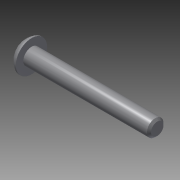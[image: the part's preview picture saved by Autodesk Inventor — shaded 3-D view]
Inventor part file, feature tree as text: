
AUTODESK INVENTOR PART (.ipt)
format: ipt  version: 2015 (Build 190159000, 159)  size: 118,784 bytes
history: native  units: in
note: dims shown in document units (in); Inventor stores cm internally (conversion verified against a paired STEP export)
features: other x3, extrude x1, chamfer x1, imported_body x1, sketch x1
ambient origin geometry x8: Origin, YZ Plane, XZ Plane, XY Plane, X Axis, Y Axis, Z Axis, Center Point
bodies: Body1 (feature_tree)
feature tree (7):
  other  "Bolt 1.25 inch"
  parser-record x1  (decoder bookkeeping rows leaked as tree rows — omitted from the tree; the rows remain in map.json)
  other  "Bolt"
  extrude  "thread length"  Depth=1.25in TaperAngle=0.0deg
  chamfer  "thread chamfer"  Distance=0.02in Angle=45.0deg
  imported_body  "Base1"
  sketch  "Sketch1"  dims[d0=0.164in d1=1.25in d2=0.0in d3=0.02in d4=0.125in d5=45.0deg d7=0.0in d9=0.0in]
